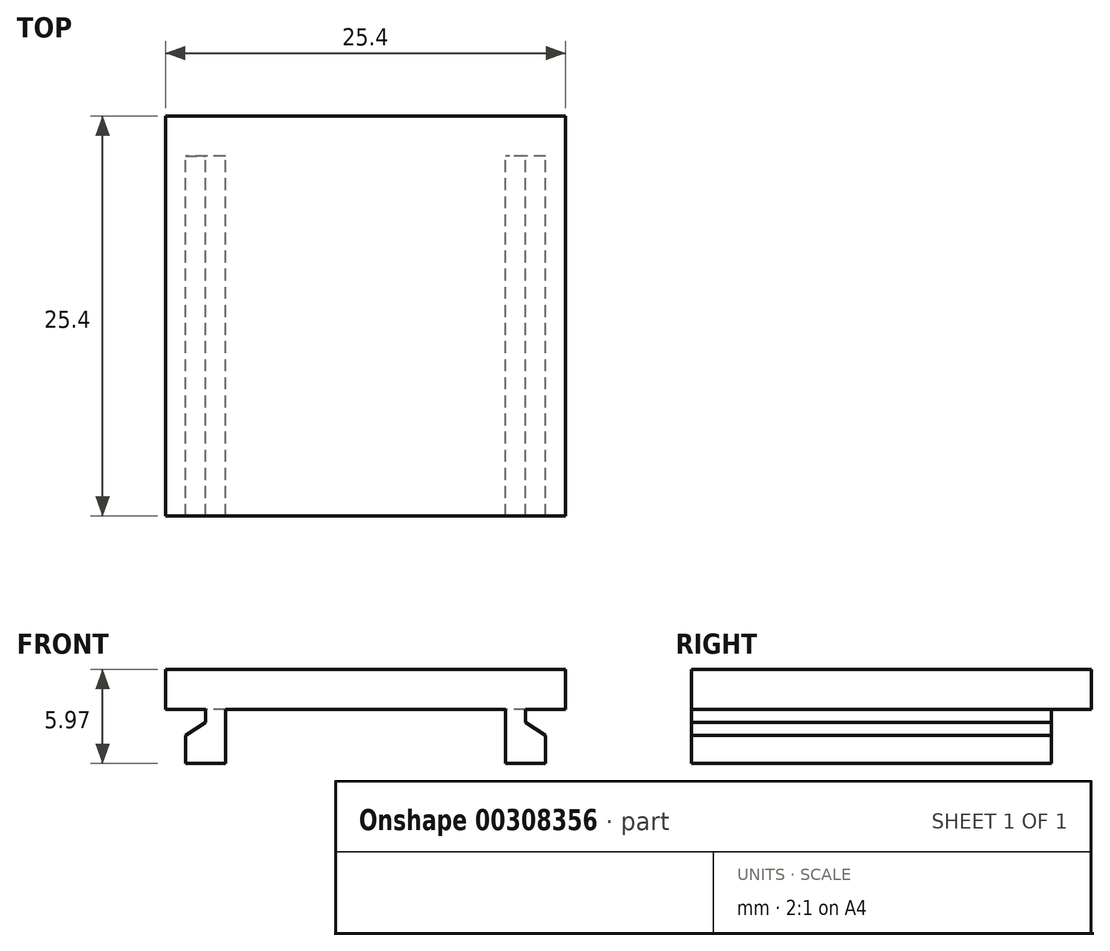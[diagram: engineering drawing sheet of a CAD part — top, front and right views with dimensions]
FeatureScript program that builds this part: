
annotation { "Feature Type Name" : "Feature", "Feature Type Description" : "" }
export const myFeature = defineFeature(function(context is Context, id is Id, definition is map)
    precondition{}
    {
        {
            var Q0;
            Q0=qCreatedBy(makeId("Top.planeOp"),FACE);
            var sketch = newSketch(context, id + "F0", { "sketchPlane" : qUnion([Q0])});
            skLineSegment(sketch, "E0.bottom", {"start": v(12.7, -12.7) * mm, "end": v(-12.7, -12.7) * mm});
            skLineSegment(sketch, "E0.top", {"start": v(12.7, 12.7) * mm, "end": v(-12.7, 12.7) * mm});
            skLineSegment(sketch, "E0.left", {"start": v(12.7, -12.7) * mm, "end": v(12.7, 12.7) * mm});
            skLineSegment(sketch, "E0.right", {"start": v(-12.7, -12.7) * mm, "end": v(-12.7, 12.7) * mm});
            skPoint(sketch, "E0.middle", {"position": v(0, 0) * mm});
            skSolve(sketch);
        }
        {
            var Q0;
            Q0=qSketchRegion(id+"F0",true);
            extrude(context, id + "F1", {"entities" : qUnion([Q0]), "oppositeDirection" : true, "depth" : 2.54 * mm});
        }
        {
            var Q0;
            Q0=qCreatedBy(makeId("Front.planeOp"),FACE);
            var sketch = newSketch(context, id + "F2", { "sketchPlane" : qUnion([Q0])});
            skLineSegment(sketch, "E1", {"start": v(-10.17, -2.54) * mm, "end": v(-10.17, -3.35) * mm});
            skLineSegment(sketch, "E2", {"start": v(10.17, -3.35) * mm, "end": v(10.17, -2.54) * mm});
            skLineSegment(sketch, "E3.bottom", {"start": v(-8.9, -5.97) * mm, "end": v(-11.44, -5.97) * mm});
            skLineSegment(sketch, "E3.right", {"start": v(-11.44, -5.97) * mm, "end": v(-11.44, -4.2) * mm});
            skLineSegment(sketch, "E4.bottom", {"start": v(11.44, -5.97) * mm, "end": v(8.9, -5.97) * mm});
            skLineSegment(sketch, "E4.left", {"start": v(11.44, -5.97) * mm, "end": v(11.44, -4.2) * mm});
            skLineSegment(sketch, "E5", {"start": v(-11.44, -4.2) * mm, "end": v(-10.17, -3.35) * mm});
            skLineSegment(sketch, "E6", {"start": v(11.44, -4.2) * mm, "end": v(10.17, -3.35) * mm});
            skLineSegment(sketch, "E7", {"start": v(-8.9, -2.54) * mm, "end": v(-10.17, -2.54) * mm});
            skLineSegment(sketch, "E8", {"start": v(8.9, -2.54) * mm, "end": v(10.17, -2.54) * mm});
            skLineSegment(sketch, "E9", {"start": v(-8.9, -5.97) * mm, "end": v(-8.9, -2.54) * mm});
            skLineSegment(sketch, "E10", {"start": v(8.9, -5.97) * mm, "end": v(8.9, -2.54) * mm});
            skSolve(sketch);
        }
        {
            var Q0;
            Q0=makeQuery(id+"F2.imprint","IMPRINT",FACE,{"disambiguationData":[TD([[makeQuery(id+"F2.imprint","IMPRINT",EDGE,{"derivedFrom":sQuery(id+"F2.wireOp",EDGE,"E1")}),1.0]])]});
            var Q1;
            Q1=makeQuery(id+"F2.imprint","IMPRINT",FACE,{"disambiguationData":[TD([[makeQuery(id+"F2.imprint","IMPRINT",EDGE,{"derivedFrom":sQuery(id+"F2.wireOp",EDGE,"E2")}),1.0]])]});
            extrude(context, id + "F3", {"entities" : qUnion([Q0, Q1]), "operationType" : NewBodyOperationType.ADD, "depth" : 25.4 * mm, "symmetric" : true});
        }
        {
            var Q0;
            Q0=qCreatedBy(makeId("Right.planeOp"),FACE);
            var sketch = newSketch(context, id + "F4", { "sketchPlane" : qUnion([Q0])});
            skLineSegment(sketch, "E11", {"start": v(0, 0) * mm, "end": v(0, -2.54) * mm});
            skLineSegment(sketch, "E12", {"start": v(12.7, -2.54) * mm, "end": v(12.7, -6.1) * mm});
            skLineSegment(sketch, "E13", {"start": v(12.7, -6.1) * mm, "end": v(10.16, -6.1) * mm});
            skLineSegment(sketch, "E14", {"start": v(10.16, -6.1) * mm, "end": v(10.16, -2.54) * mm});
            skLineSegment(sketch, "E15", {"start": v(10.16, -2.54) * mm, "end": v(12.7, -2.54) * mm});
            skSolve(sketch);
        }
        {
            var Q0;
            Q0=qSketchRegion(id+"F4",true);
            extrude(context, id + "F5", {"entities" : qUnion([Q0]), "operationType" : NewBodyOperationType.REMOVE, "depth" : 25.4 * mm, "symmetric" : true});
        }
    });
